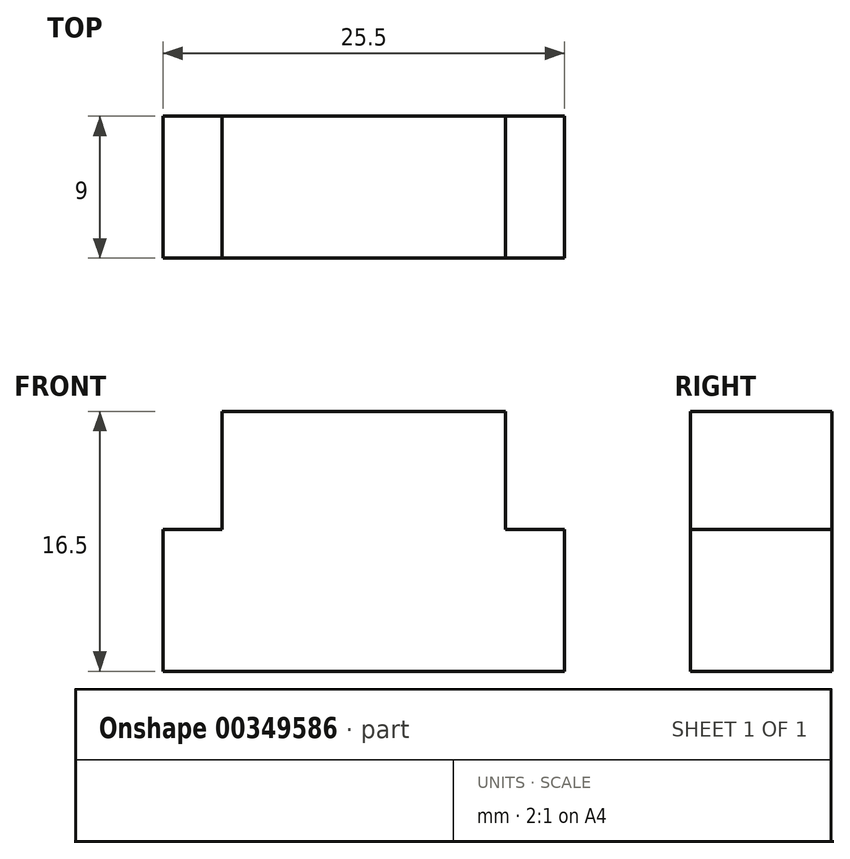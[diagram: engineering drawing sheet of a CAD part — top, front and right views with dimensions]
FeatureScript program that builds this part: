
annotation { "Feature Type Name" : "Feature", "Feature Type Description" : "" }
export const myFeature = defineFeature(function(context is Context, id is Id, definition is map)
    precondition{}
    {
        {
            var Q0;
            Q0=qCreatedBy(makeId("Front.planeOp"),FACE);
            var sketch = newSketch(context, id + "F0", { "sketchPlane" : qUnion([Q0])});
            skLineSegment(sketch, "E0.bottom", {"start": v(-0.85, 0) * mm, "end": v(0.85, 0) * mm});
            skLineSegment(sketch, "E0.top", {"start": v(-0.85, -0.6) * mm, "end": v(0.85, -0.6) * mm});
            skLineSegment(sketch, "E0.left", {"start": v(-0.85, 0) * mm, "end": v(-0.85, -0.6) * mm});
            skLineSegment(sketch, "E0.right", {"start": v(0.85, 0) * mm, "end": v(0.85, -0.6) * mm});
            skLineSegment(sketch, "E1.bottom", {"start": v(-0.6, 0) * mm, "end": v(0.6, 0) * mm});
            skLineSegment(sketch, "E1.top", {"start": v(-0.6, 0.5) * mm, "end": v(0.6, 0.5) * mm});
            skLineSegment(sketch, "E1.left", {"start": v(0.6, 0) * mm, "end": v(0.6, 0.5) * mm});
            skLineSegment(sketch, "E1.right", {"start": v(-0.6, 0) * mm, "end": v(-0.6, 0.5) * mm});
            skSolve(sketch);
        }
        {
            var Q0;
            Q0=qSketchRegion(id+"F0",true);
            extrude(context, id + "F1", {"entities" : qUnion([Q0]), "endBound" : BoundingType.SYMMETRIC, "depth" : .6 * mm});
        }
        {
            var Q0;
            Q0=makeQuery(id+"F1.opExtrude","SWEPT_BODY",BODY,{"disambiguationData":[OSD([sQuery(id+"F0.wireOp",EDGE,"E0.bottom"),sQuery(id+"F0.wireOp",EDGE,"E0.top"),sQuery(id+"F0.wireOp",EDGE,"E0.left"),sQuery(id+"F0.wireOp",EDGE,"E0.right"),sQuery(id+"F0.wireOp",EDGE,"E1.top"),sQuery(id+"F0.wireOp",EDGE,"E1.left"),sQuery(id+"F0.wireOp",EDGE,"E1.right")])]});
            var Q1;
            Q1=qCreatedBy(makeId("Origin.pointOp"),VERTEX);
            transform(context, id + "F2", {"entities" : qUnion([Q0]), "transformType" : TransformType.SCALE_UNIFORMLY, "scale" : 15, "scalePoint" : qUnion([Q1]), "makeCopy" : false});
        }
    });
